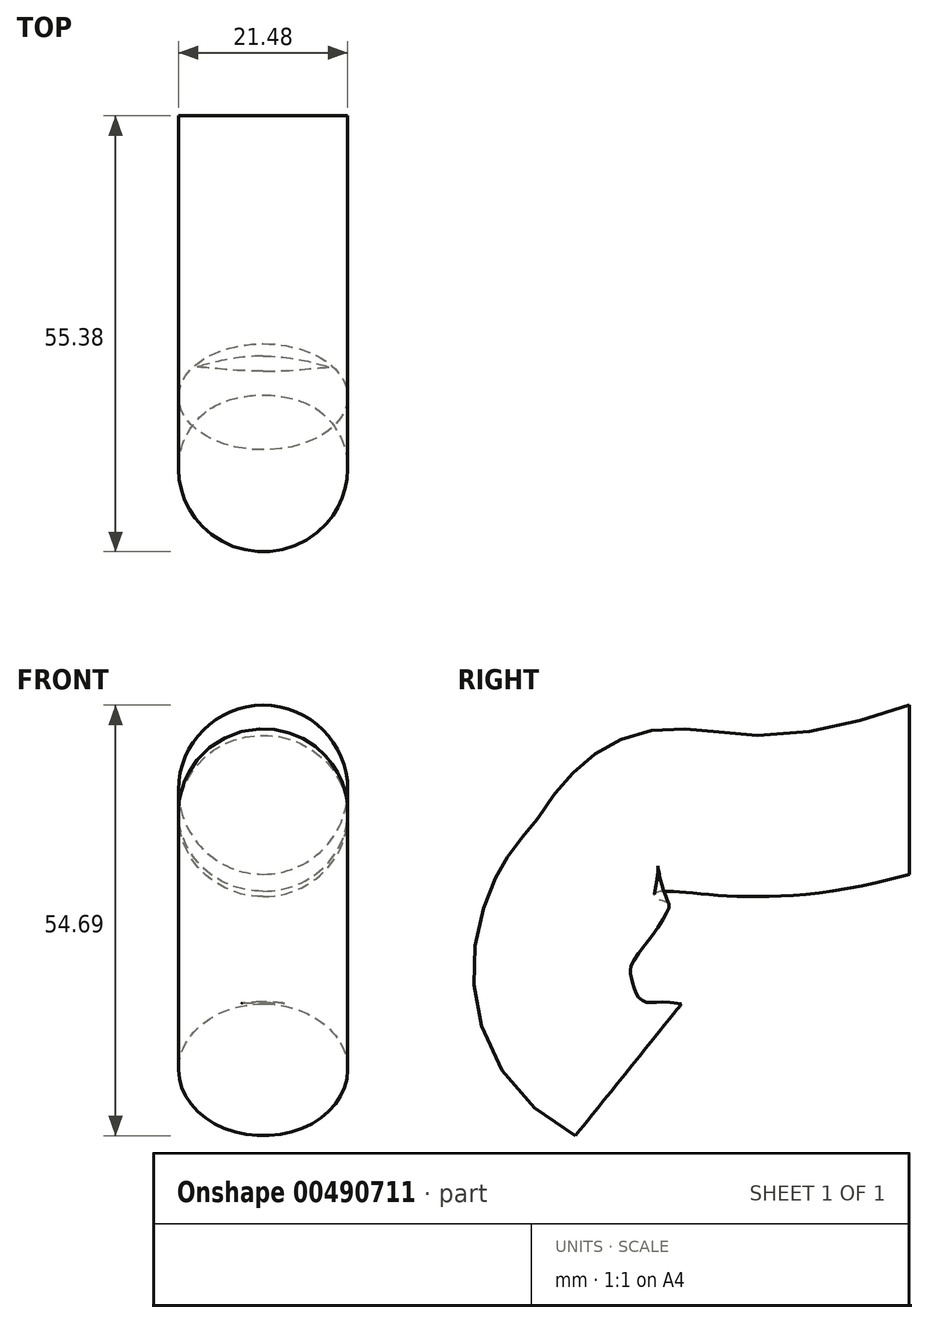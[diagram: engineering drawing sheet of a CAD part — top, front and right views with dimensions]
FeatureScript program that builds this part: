
annotation { "Feature Type Name" : "Feature", "Feature Type Description" : "" }
export const myFeature = defineFeature(function(context is Context, id is Id, definition is map)
    precondition{}
    {
        {
            var Q0;
            Q0=qCreatedBy(makeId("Front.planeOp"),FACE);
            var sketch = newSketch(context, id + "F0", { "sketchPlane" : qUnion([Q0])});
            skCircle(sketch, "E0", {"center": v(0, 35.34) * mm, "radius": 10.74 * mm});
            skSolve(sketch);
        }
        {
            var Q0;
            Q0=qCreatedBy(makeId("Right.planeOp"),FACE);
            var sketch = newSketch(context, id + "F1", { "sketchPlane" : qUnion([Q0])});
            skFitSpline(sketch, "E1", {"points": [v(-35.52, 0) * mm, v(-44, 16.66) * mm, v(-39.67, 24.2) * mm, v(-32.6, 31.66) * mm, v(0, 35.02) * mm], "startDerivative": vector(-108.7, 43.19) * mm, "endDerivative": vector(170.55, 52.72) * mm});
            skSolve(sketch);
        }
        {
            var Q0;
            Q0 = qSketchRegion(id + "F0", true);
            var Q1;
            Q1 = qConstructionFilter(qBodyType(qCreatedBy(id + "F1" ,EDGE), BodyType.WIRE), ConstructionObject.NO);
            sweep(context, id + "F2", {"profiles" : qUnion([Q0]), "path" : qUnion([Q1])});
        }
    });
